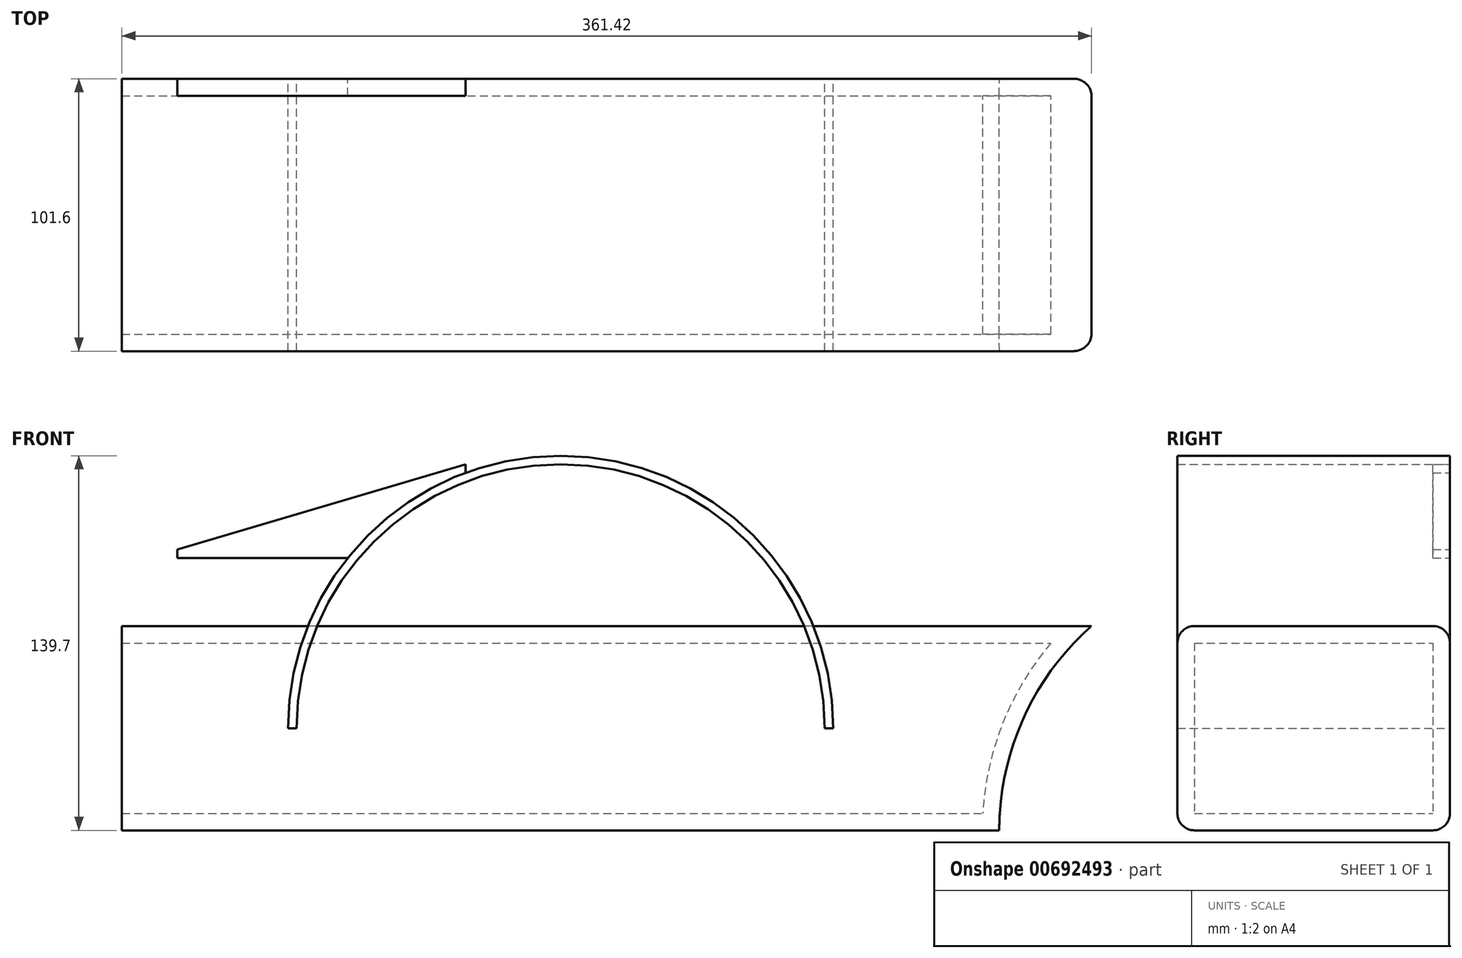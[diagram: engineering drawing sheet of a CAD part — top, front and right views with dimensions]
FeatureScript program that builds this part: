
annotation { "Feature Type Name" : "Feature", "Feature Type Description" : "" }
export const myFeature = defineFeature(function(context is Context, id is Id, definition is map)
    precondition{}
    {
        {
            var Q0;
            Q0=qCreatedBy(makeId("Front.planeOp"),FACE);
            var sketch = newSketch(context, id + "F0", { "sketchPlane" : qUnion([Q0])});
            skLineSegment(sketch, "E0.bottom", {"start": v(163.51, 38.1) * mm, "end": v(-163.51, 38.1) * mm});
            skLineSegment(sketch, "E0.top", {"start": v(163.51, -38.1) * mm, "end": v(-163.51, -38.1) * mm});
            skLineSegment(sketch, "E0.right", {"start": v(-163.51, 38.1) * mm, "end": v(-163.51, -38.1) * mm});
            skPoint(sketch, "E0.middle", {"position": v(0, 0) * mm});
            skArc(sketch, "E1", {"start": v(197.91, 38.1) * mm, "mid": v(172.51, 3.7) * mm, "end": v(163.51, -38.1) * mm});
            skLineSegment(sketch, "E2", {"start": v(163.51, 38.1) * mm, "end": v(197.91, 38.1) * mm});
            skLineSegment(sketch, "E3", {"start": v(0, 0) * mm, "end": v(0, 38.1) * mm, "construction": true});
            skLineSegment(sketch, "E4", {"start": v(0, 0) * mm, "end": v(-163.51, 0) * mm, "construction": true});
            skSolve(sketch);
        }
        {
            var Q0;
            Q0=makeQuery(id+"F0.imprint","IMPRINT",FACE,{"disambiguationData":[TD([[makeQuery(id+"F0.imprint","IMPRINT",EDGE,{"derivedFrom":sQuery(id+"F0.wireOp",EDGE,"E0.bottom")}),1.0]])]});
            extrude(context, id + "F1", {"entities" : qUnion([Q0]), "depth" : 101.6 * mm, "offsetDistance" : 25.4 * mm});
        }
        {
            var Q0;
            Q0=makeQuery(id+"F1.opExtrude","CAP_EDGE",EDGE,{"disambiguationData":[OSD([sQuery(id+"F0.wireOp",EDGE,"E0.bottom"),sQuery(id+"F0.wireOp",EDGE,"E2")])],"isStart":false});
            var Q1;
            Q1=makeQuery(id+"F1.opExtrude","CAP_EDGE",EDGE,{"disambiguationData":[OSD([sQuery(id+"F0.wireOp",EDGE,"E0.top")])],"isStart":false});
            var Q2;
            Q2=makeQuery(id+"F1.opExtrude","CAP_EDGE",EDGE,{"disambiguationData":[OSD([sQuery(id+"F0.wireOp",EDGE,"E0.bottom"),sQuery(id+"F0.wireOp",EDGE,"E2")])],"isStart":true});
            var Q3;
            Q3=makeQuery(id+"F1.opExtrude","CAP_EDGE",EDGE,{"disambiguationData":[OSD([sQuery(id+"F0.wireOp",EDGE,"E0.top")])],"isStart":true});
            fillet(context, id + "F2", {"entities" : qUnion([Q0, Q1, Q2, Q3]), "radius" : 6.35 * mm, "tangentPropagation" : true, "allowEdgeOverflow" : false});
        }
        {
            var Q0;
            Q0=makeQuery(id+"F1.opExtrude","SWEPT_FACE",FACE,{"disambiguationData":[OSD([sQuery(id+"F0.wireOp",EDGE,"E0.right")])]});
            shell(context, id + "F3", {"entities" : qUnion([Q0]), "thickness" : 6.35 * mm});
        }
        {
            var Q0;
            Q0=qCreatedBy(makeId("Front.planeOp"),FACE);
            var sketch = newSketch(context, id + "F4", { "sketchPlane" : qUnion([Q0])});
            skArc(sketch, "E5", {"start": v(101.6, 0) * mm, "mid": v(0, 101.6) * mm, "end": v(-101.6, 0) * mm});
            skArc(sketch, "E6", {"start": v(98.43, 0) * mm, "mid": v(0, 98.43) * mm, "end": v(-98.43, 0) * mm});
            skLineSegment(sketch, "E7", {"start": v(101.6, 0) * mm, "end": v(98.43, 0) * mm});
            skLineSegment(sketch, "E8.trimOffspring", {"start": v(-98.43, 0) * mm, "end": v(-101.6, 0) * mm});
            skSolve(sketch);
        }
        {
            var Q0;
            Q0 = qSketchRegion(id + "F4", true);
            extrude(context, id + "F5", {"entities" : qUnion([Q0]), "depth" : 101.6 * mm, "offsetDistance" : 25.4 * mm});
        }
        {
            var Q0;
            Q0=qCreatedBy(makeId("Front.planeOp"),FACE);
            var sketch = newSketch(context, id + "F6", { "sketchPlane" : qUnion([Q0])});
            skArc(sketch, "E9", {"start": v(-35.36, 95.25) * mm, "mid": v(-59.5, 82.36) * mm, "end": v(-79.31, 63.5) * mm});
            skLineSegment(sketch, "E10", {"start": v(-79.31, 63.5) * mm, "end": v(-142.81, 63.5) * mm});
            skLineSegment(sketch, "E11", {"start": v(-142.81, 63.5) * mm, "end": v(-142.81, 66.68) * mm});
            skLineSegment(sketch, "E12", {"start": v(-35.36, 95.25) * mm, "end": v(-35.36, 98.43) * mm});
            skLineSegment(sketch, "E13", {"start": v(-142.81, 66.68) * mm, "end": v(-35.36, 98.43) * mm});
            skSolve(sketch);
        }
        {
            var Q0;
            Q0=makeQuery(id+"F6.imprint","IMPRINT",FACE,{"disambiguationData":[TD([[makeQuery(id+"F6.imprint","IMPRINT",EDGE,{"derivedFrom":sQuery(id+"F6.wireOp",EDGE,"E9")}),-1.0]])]});
            extrude(context, id + "F7", {"entities" : qUnion([Q0]), "depth" : 6.35 * mm, "offsetDistance" : 25.4 * mm});
        }
    });
